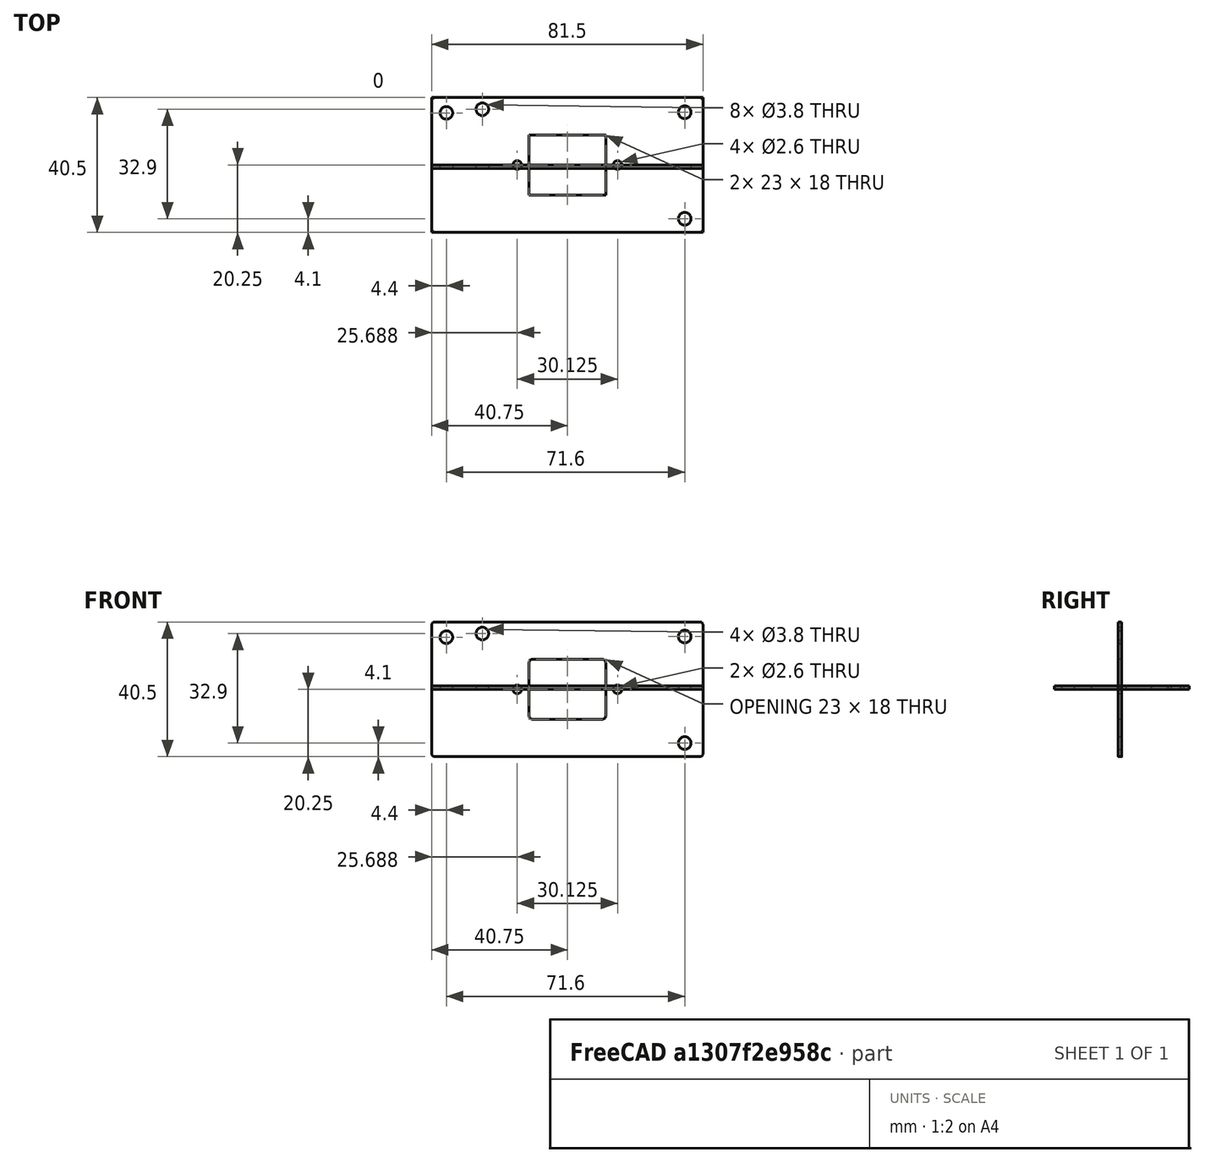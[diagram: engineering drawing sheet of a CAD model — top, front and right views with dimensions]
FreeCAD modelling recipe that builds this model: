
FCSTD DOCUMENT  (FreeCAD 0.20R)
Label: flex_panel
License: All rights reserved
LicenseURL: http://en.wikipedia.org/wiki/All_rights_reserved
objects: TechDraw::DrawViewPart×3, TechDraw::DrawViewDimension×3, Part::Fillet×2, Sketcher::SketchObject×1, Image::ImagePlane×1, Part::Extrusion×1, TechDraw::DrawSVGTemplate×1, TechDraw::DrawPage×1, Part::Part2DObjectPython×1
note: 5 computed .brp shape members not serialized (recipe doc carries the construction recipe); baked Part::Feature solids carry a one-line shape summary decoded from their .brp

FEATURE [Sketcher::SketchObject] Sketch  label="Plate_sketch"
  FullyConstrained = true
  sketch-geometry (14):
    g0: LineSegment StartX=-40.75 StartY=20.25 StartZ=0 EndX=40.75 EndY=20.25 EndZ=0
    g1: LineSegment StartX=40.75 StartY=20.25 StartZ=0 EndX=40.75 EndY=-20.25 EndZ=0
    g2: LineSegment StartX=40.75 StartY=-20.25 StartZ=0 EndX=-40.75 EndY=-20.25 EndZ=0
    g3: LineSegment StartX=-40.75 StartY=-20.25 StartZ=0 EndX=-40.75 EndY=20.25 EndZ=0
    g4: Circle CenterX=-36.35 CenterY=15.65 CenterZ=0 NormalX=0 NormalY=0 NormalZ=1 AngleXU=0 Radius=1.89865
    g5: Circle CenterX=-25.55 CenterY=16.75 CenterZ=0 NormalX=0 NormalY=0 NormalZ=1 AngleXU=0 Radius=1.89865
    g6: Circle CenterX=35.25 CenterY=-16.15 CenterZ=0 NormalX=0 NormalY=0 NormalZ=1 AngleXU=0 Radius=1.89865
    g7: Circle CenterX=35.25 CenterY=15.85 CenterZ=0 NormalX=0 NormalY=0 NormalZ=1 AngleXU=0 Radius=1.89865
    g8: LineSegment StartX=-11.5 StartY=9 StartZ=0 EndX=11.5 EndY=9 EndZ=0
    g9: LineSegment StartX=11.5 StartY=9 StartZ=0 EndX=11.5 EndY=-9 EndZ=0
    g10: LineSegment StartX=11.5 StartY=-9 StartZ=0 EndX=-11.5 EndY=-9 EndZ=0
    g11: LineSegment StartX=-11.5 StartY=-9 StartZ=0 EndX=-11.5 EndY=9 EndZ=0
    g12: Circle CenterX=-15.0625 CenterY=0 CenterZ=0 NormalX=0 NormalY=0 NormalZ=1 AngleXU=0 Radius=1.3
    g13: Circle CenterX=15.0625 CenterY=0 CenterZ=0 NormalX=0 NormalY=0 NormalZ=1 AngleXU=0 Radius=1.3
  constraints (38):
    c: Coincident(g0,g1)
    c: Coincident(g1,g2)
    c: Coincident(g2,g3)
    c: Coincident(g3,g0)
    c: Horizontal(g0)
    c: Horizontal(g2)
    c: Vertical(g1)
    c: Vertical(g3)
    c: Symmetric(g0,g1,g-1)
    c: DistanceX(g0,g0) = 81.5  'Width'
    c: DistanceY(g1,g1) = 40.5  'Height'
    c: Diameter(g4) = 3.7973  '6-31 free fit'
    c: Diameter(g5) = 3.7973
    c: Equal(g6,g7)
    c: Diameter(g6) = 3.7973
    c: DistanceX(g0,g4) = 4.4
    c: DistanceX(g0,g5) = 15.2
    c: DistanceY(g6,g7) = 32
    c: DistanceY(g2,g4) = 35.9
    c: DistanceY(g2,g5) = 37
    c: DistanceY(g1,g6) = 4.1
    c: DistanceX(g0,g7) = 76
    c: Vertical(g6,g7)
    c: Coincident(g8,g9)
    c: Coincident(g9,g10)
    c: Coincident(g10,g11)
    c: Coincident(g11,g8)
    c: Horizontal(g8)
    c: Vertical(g11)
    c: DistanceY(g11,g11) = 18
    c: DistanceX(g8,g8) = 23
    c: Diameter(g12) = 2.6
    c: Diameter(g13) = 2.6
    c: DistanceX(g12,g13) = 30.125
    c: Horizontal(g12,g-1)
    c: Symmetric(g12,g13,g-2)
    c: Symmetric(g10,g9,g-2)
    c: Symmetric(g8,g9,g-1)
FEATURE [Image::ImagePlane] ImagePlane
  Placement = pos=(-10.5,-3,0) rot=(0,0,1;0rad)
  XSize = 138.25
  YSize = 80.2
FEATURE [Part::Extrusion] Extrude001  label="Plate_extrude"
  Base = -> Sketch
  Dir = (0,0,1)
  DirMode = 2
  FaceMakerClass = Part::FaceMakerBullseye
  LengthFwd = 1
  LengthRev = 0
  Solid = true
  Symmetric = false
FEATURE [Part::Fillet] Fillet  label="Plate_outer_fillet"
  Base = -> Extrude001
  Edges = 4 edges r=1: [Edge1,Edge2,Edge5,Edge8]
FEATURE [Part::Fillet] Fillet001  label="Plate"
  Base = -> Fillet
  Edges = 4 edges r=1: [Edge45,Edge46,Edge47,Edge48]
  Placement = pos=(0,0,0) rot=(1,0,0;1.5708rad)
FEATURE [TechDraw::DrawSVGTemplate] Template
  EditableTexts = Designed_by_Name=Designed by Name; Drawing_number=Drawing number; FC-Date=Date; FC-SC=Scale; FC-SH=Sheet; FC-Title=Title; Subtitle=Subtitle; Weight=Weight
  Height = 210
  Orientation = 1
  Width = 297
FEATURE [TechDraw::DrawViewPart] View  label="Exterior face"
  CoarseView = false
  Direction = (0,-1,0)
  Focus = 100
  HardHidden = false
  IsoCount = 0
  IsoHidden = false
  IsoVisible = false
  LockPosition = false
  Perspective = false
  Rotation = 0
  ScaleType = 0
  SeamHidden = false
  SeamVisible = true
  SmoothHidden = false
  SmoothVisible = true
  Source = -> [Fillet001]
  X = 77.8671
  XDirection = (1,0,0)
  Y = 147.911
FEATURE [TechDraw::DrawViewPart] View001  label="Interior face"
  CoarseView = false
  Direction = (0,1,0)
  Focus = 100
  HardHidden = false
  IsoCount = 0
  IsoHidden = false
  IsoVisible = false
  LockPosition = false
  Perspective = false
  Rotation = 0
  ScaleType = 0
  SeamHidden = false
  SeamVisible = true
  SmoothHidden = false
  SmoothVisible = true
  Source = -> [Fillet001]
  X = 205.462
  XDirection = (-1,0,0)
  Y = 150.19
FEATURE [TechDraw::DrawViewPart] View002  label="Side view [1mm thick]"
  CoarseView = false
  Direction = (1,0,0)
  Focus = 100
  HardHidden = false
  IsoCount = 0
  IsoHidden = false
  IsoVisible = false
  LockPosition = false
  Perspective = false
  Rotation = 0
  ScaleType = 0
  SeamHidden = false
  SeamVisible = true
  SmoothHidden = false
  SmoothVisible = true
  Source = -> [Fillet001]
  X = 71.4114
  XDirection = (0,1,0)
  Y = 59.4304
FEATURE [TechDraw::DrawViewDimension] Dimension
  AngleOverride = false
  Arbitrary = false
  ArbitraryTolerances = false
  EqualTolerance = true
  ExtensionAngle = 0
  FormatSpec = %.2w
  FormatSpecOverTolerance = %+.2w
  FormatSpecUnderTolerance = %+.2w
  Inverted = false
  LineAngle = 0
  LockPosition = false
  MeasureType = 1
  OverTolerance = 0
  References2D = -> [View001]
  Rotation = 0
  ScaleType = 0
  TheoreticalExact = false
  Type = 0
  UnderTolerance = 0
  X = -0.722208
  Y = 18.1943
FEATURE [TechDraw::DrawViewDimension] Dimension001
  AngleOverride = false
  Arbitrary = false
  ArbitraryTolerances = false
  EqualTolerance = true
  ExtensionAngle = 0
  FormatSpec = %.2w
  FormatSpecOverTolerance = %+.2w
  FormatSpecUnderTolerance = %+.2w
  Inverted = false
  LineAngle = 0
  LockPosition = false
  MeasureType = 1
  OverTolerance = 0
  References2D = -> [View001]
  Rotation = 0
  ScaleType = 0
  TheoreticalExact = false
  Type = 2
  UnderTolerance = 0
  X = -24.6475
  Y = 4.90736
FEATURE [TechDraw::DrawViewDimension] Dimension002
  AngleOverride = false
  Arbitrary = false
  ArbitraryTolerances = false
  EqualTolerance = true
  ExtensionAngle = 0
  FormatSpec = %.2w
  FormatSpecOverTolerance = %+.2w
  FormatSpecUnderTolerance = %+.2w
  Inverted = false
  LineAngle = 0
  LockPosition = false
  MeasureType = 1
  OverTolerance = 0
  References2D = -> [View001]
  Rotation = 0
  ScaleType = 0
  TheoreticalExact = false
  Type = 1
  UnderTolerance = 0
  X = -1.23644
  Y = -9.56715
FEATURE [TechDraw::DrawPage] Page
  KeepUpdated = true
  NextBalloonIndex = 1
  ProjectionType = 0
  Template = -> Template
  Views = -> [View,View001,View002,Dimension,Dimension001,Dimension002]
FEATURE [Part::Part2DObjectPython] Shape2DView  # Draft 2D object (typed FeaturePython)
  AutoUpdate = true
  Base = -> Fillet001
  Clip = false
  FaceNumbers = [23]
  FuseArch = false
  HiddenLines = false
  InPlace = true
  OnlySolids = false
  Placement = pos=(0,0,0) rot=(1,0,0;1.5708rad)
  Projection = (0,-1,0)
  ProjectionMode = 0
  SegmentLength = 0.05
  Tessellation = false
  VisibleOnly = false
